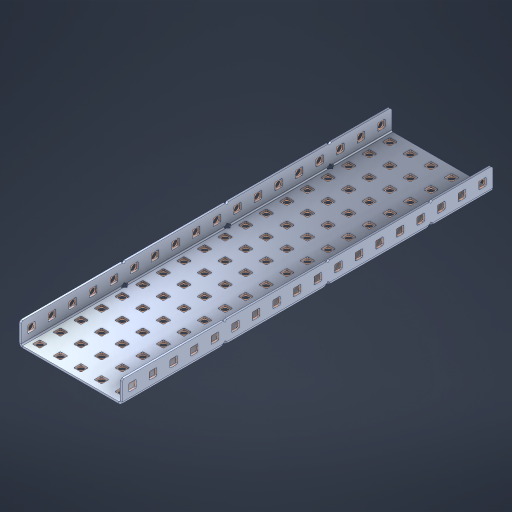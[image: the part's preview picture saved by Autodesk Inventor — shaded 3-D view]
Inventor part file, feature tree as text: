
AUTODESK INVENTOR PART (.ipt)
format: ipt  version: 2023 (Build 270158000, 158)  size: 1,547,264 bytes
history: native  units: in
note: dims shown in document units (in); Inventor stores cm internally (conversion verified against a paired STEP export)
features: other x131, extrude x125, sheet_metal_op x10, sketch x8, mirror x1, pattern_linear x1, chamfer x1
ambient origin geometry x8: Origin, YZ Plane, XZ Plane, XY Plane, X Axis, Y Axis, Z Axis, Center Point
bodies: Solid1 (feature_tree), Body (feature_tree)
feature tree (277):
  other  "Flange Pattern Plane"
  sheet_metal_op  "Flange Pattern"
  sheet_metal_op  "Body Pattern"
  other  "Arc Length"
  mirror  "Notch Mirror"
  pattern_linear  "Notch Pattern"  Spacing1=0.1875in  [1 undecoded]
  chamfer  "End Chamfer"
  extrude  "Half Cut"  Depth=0.0469in
  sketch  "Sketch1"  dims[d0=2.5in]
  other  "Plate1"
  sketch  "Sketch2"  dims[d1=9.0in]
  other  "Plate2"
  sheet_metal_op  "Bend1"
  sheet_metal_op  "Corner1"
  sketch  "Sketch3"  dims[d2=0.0469in]
  other  "Flange Pattern Sketch"
  sketch  "Sketch7"  dims[d3=0.0469in]
  other  "Srf1"
  other  "Srf2"
  sketch  "Sketch8"  dims[d4=0.0234in]
  sketch  "Sketch9"  dims[d5=0.0938in]
  other  "Srf91"
  sheet_metal_op  "Body Pattern Sketch"
  other  "Srf92"
  sketch  "Sketch13"  dims[d6=0.0469in]
  sketch  "Sketch14"  dims[d7=0.5in d8=90.0deg d9=0.0312in d10=0.1875in d11=0.0469in d12=0.0469in d16=0.182in d17=0.02in d18=0.0469in d19=0.0in d20=0.25in d21=0.25in d46=0.172in d47=1.0in d48=0.0in d49=0.182in d50=0.02in d51=0.25in d52=0.25in d53=0.0469in d54=0.0in d55=0.172in d56=1.0in d57=0.0in d60=7.0866in d62=0.5in d63=1.9685in d65=0.5in d85=0.1227in d86=0.1659in d88=0.04in d89=0.0469in d90=0.0in d91=0.04in d92=0.0491in d95=2.5in d96=0.04in d97=0.25in d98=45.0deg d101=0.0in d102=2.497in d131=2.5in d132=7.0866in d134=0.5in d139=0.5in]
  other  "Srf856"
  other  "Srf1310"
  other  "Srf1311"
  other  "Srf1312"
  other  "Srf1376"
  other  "Srf1377"
  other  "Srf1728"
  other  "Srf1755"
  other  "Srf1878"
  other  "Srf1879"
  other  "Srf1880"
  other  "Srf1881"
  other  "Srf1882"
  other  "Srf1883"
  other  "Srf1884"
  other  "Srf1885"
  other  "Srf1886"
  other  "Srf1887"
  other  "Srf1888"
  other  "Srf1889"
  other  "Srf1890"
  other  "Srf1891"
  other  "Srf1892"
  other  "Srf1893"
  other  "Srf1894"
  other  "Srf1895"
  other  "Srf1896"
  other  "Srf1897"
  other  "Srf1898"
  other  "Srf1899"
  other  "Srf1900"
  other  "Srf1901"
  other  "Srf1902"
  other  "Srf1903"
  other  "Srf1904"
  other  "Srf1905"
  other  "Srf1906"
  other  "Srf1942"
  other  "Srf1943"
  other  "Srf1944"
  other  "Srf1945"
  other  "Srf1946"
  other  "Srf1947"
  other  "Srf1948"
  other  "Srf1949"
  other  "Srf1950"
  other  "Srf1951"
  other  "Srf1952"
  other  "Srf1953"
  other  "Srf1954"
  other  "Srf1955"
  other  "Srf1956"
  other  "Srf1957"
  other  "Srf1958"
  other  "Srf1959"
  other  "Srf1960"
  other  "Srf1961"
  other  "Srf1962"
  other  "Srf1963"
  other  "Srf1964"
  other  "Srf1965"
  other  "Srf1966"
  other  "Srf1967"
  other  "Srf1968"
  other  "Srf1969"
  other  "Srf1970"
  other  "Srf2111"
  other  "Srf2146"
  other  "Srf2147"
  other  "Srf2148"
  other  "Srf2149"
  other  "Srf2150"
  other  "Srf2151"
  other  "Srf2152"
  other  "Srf2153"
  other  "Srf2154"
  other  "Srf2155"
  other  "Srf2156"
  other  "Srf2157"
  other  "Srf2158"
  other  "Srf2159"
  other  "Srf2160"
  other  "Srf2161"
  other  "Srf2162"
  other  "Srf2163"
  other  "Srf2164"
  other  "Srf2165"
  other  "Srf2166"
  other  "Srf2167"
  other  "Srf2168"
  other  "Srf2169"
  other  "Srf2170"
  other  "Srf2171"
  other  "Srf2172"
  other  "Srf2173"
  other  "Srf2174"
  other  "Srf2175"
  other  "Srf2176"
  other  "Srf2177"
  other  "Srf2178"
  other  "Srf2179"
  other  "Srf2180"
  other  "Srf2181"
  other  "Srf2182"
  other  "Srf2183"
  other  "Srf2184"
  other  "Srf2185"
  other  "Srf2186"
  other  "Srf2187"
  other  "Srf2188"
  other  "Srf2189"
  other  "Srf2190"
  other  "Srf2191"
  other  "Srf2192"
  other  "Srf2193"
  other  "Srf2194"
  other  "Srf2195"
  other  "Srf2196"
  other  "Srf2197"
  other  "Srf2198"
  other  "Srf2199"
  other  "Srf2200"
  sheet_metal_op  "Flange Stamp"
  sheet_metal_op  "Flange Circle"
  sheet_metal_op  "Body Stamp"
  sheet_metal_op  "Body Circle"
  sheet_metal_op  "Notch"
  extrude  "ExtrusionSrf2"  Depth=0.0469in
  extrude  "ExtrusionSrf92"  Depth=2.5in
  extrude  "ExtrusionSrf856"  Depth=0.02in
  extrude  "ExtrusionSrf1310"  Depth=0.0469in
  extrude  "ExtrusionSrf1311"  TaperAngle=0.0deg  [1 undecoded]
  extrude  "ExtrusionSrf1312"  Depth=0.25in
  extrude  "ExtrusionSrf1376"  Depth=0.25in
  extrude  "ExtrusionSrf1377"  Depth=2.5in
  extrude  "ExtrusionSrf1728"  Depth=2.5in TaperAngle=0.0deg
  extrude  "ExtrusionSrf1755"  Depth=2.5in
  extrude  "ExtrusionSrf1878"  Depth=0.02in
  extrude  "ExtrusionSrf1879"  Depth=0.25in
  extrude  "ExtrusionSrf1880"  Depth=0.25in
  extrude  "ExtrusionSrf1881"  Depth=0.0469in
  extrude  "ExtrusionSrf1882"  TaperAngle=0.0deg  [1 undecoded]
  extrude  "ExtrusionSrf1883"  Depth=2.5in
  extrude  "ExtrusionSrf1884"  Depth=2.5in TaperAngle=0.0deg
  extrude  "ExtrusionSrf1885"  Depth=2.5in
  extrude  "ExtrusionSrf1886"  Depth=2.5in
  extrude  "ExtrusionSrf1887"  Depth=2.5in
  extrude  "ExtrusionSrf1888"  Depth=2.5in
  extrude  "ExtrusionSrf1889"  Depth=2.5in
  extrude  "ExtrusionSrf1890"  Depth=0.0469in
  extrude  "ExtrusionSrf1891"  TaperAngle=0.0deg  [1 undecoded]
  extrude  "ExtrusionSrf1892"  Depth=2.5in
  extrude  "ExtrusionSrf1893"  Depth=2.5in
  extrude  "ExtrusionSrf1894"  Depth=2.5in
  extrude  "ExtrusionSrf1895"  Depth=0.25in TaperAngle=45.0deg
  extrude  "ExtrusionSrf1896"  TaperAngle=0.0deg  [1 undecoded]
  extrude  "ExtrusionSrf1897"  Depth=2.5in
  extrude  "ExtrusionSrf1898"  Depth=2.5in
  extrude  "ExtrusionSrf1899"  Depth=2.5in
  extrude  "ExtrusionSrf1900"  Depth=2.5in
  extrude  "ExtrusionSrf1901"  Depth=2.5in
  extrude  "ExtrusionSrf1902"  [1 undecoded]
  extrude  "ExtrusionSrf1903"  [1 undecoded]
  extrude  "ExtrusionSrf1904"  [1 undecoded]
  extrude  "ExtrusionSrf1905"  [1 undecoded]
  extrude  "ExtrusionSrf1906"  [1 undecoded]
  extrude  "ExtrusionSrf1942"  [1 undecoded]
  extrude  "ExtrusionSrf1943"  [1 undecoded]
  extrude  "ExtrusionSrf1944"  [1 undecoded]
  extrude  "ExtrusionSrf1945"  [1 undecoded]
  extrude  "ExtrusionSrf1946"  [1 undecoded]
  extrude  "ExtrusionSrf1947"  [1 undecoded]
  extrude  "ExtrusionSrf1948"  [1 undecoded]
  extrude  "ExtrusionSrf1949"  [1 undecoded]
  extrude  "ExtrusionSrf1950"  [1 undecoded]
  extrude  "ExtrusionSrf1951"  [1 undecoded]
  extrude  "ExtrusionSrf1952"  [1 undecoded]
  extrude  "ExtrusionSrf1953"  [1 undecoded]
  extrude  "ExtrusionSrf1954"  [1 undecoded]
  extrude  "ExtrusionSrf1955"  [1 undecoded]
  extrude  "ExtrusionSrf1956"  [1 undecoded]
  extrude  "ExtrusionSrf1957"  [1 undecoded]
  extrude  "ExtrusionSrf1958"  [1 undecoded]
  extrude  "ExtrusionSrf1959"  [1 undecoded]
  extrude  "ExtrusionSrf1960"  [1 undecoded]
  extrude  "ExtrusionSrf1961"  [1 undecoded]
  extrude  "ExtrusionSrf1962"  [1 undecoded]
  extrude  "ExtrusionSrf1963"  [1 undecoded]
  extrude  "ExtrusionSrf1964"  [1 undecoded]
  extrude  "ExtrusionSrf1965"  [1 undecoded]
  extrude  "ExtrusionSrf1966"  [1 undecoded]
  extrude  "ExtrusionSrf1967"  [1 undecoded]
  extrude  "ExtrusionSrf1968"  [1 undecoded]
  extrude  "ExtrusionSrf1969"  [1 undecoded]
  extrude  "ExtrusionSrf1970"  [1 undecoded]
  extrude  "ExtrusionSrf2111"  [1 undecoded]
  extrude  "ExtrusionSrf2146"  [1 undecoded]
  extrude  "ExtrusionSrf2147"  [1 undecoded]
  extrude  "ExtrusionSrf2148"  [1 undecoded]
  extrude  "ExtrusionSrf2149"  [1 undecoded]
  extrude  "ExtrusionSrf2150"  [1 undecoded]
  extrude  "ExtrusionSrf2151"  [1 undecoded]
  extrude  "ExtrusionSrf2152"  [1 undecoded]
  extrude  "ExtrusionSrf2153"  [1 undecoded]
  extrude  "ExtrusionSrf2154"  [1 undecoded]
  extrude  "ExtrusionSrf2155"  [1 undecoded]
  extrude  "ExtrusionSrf2156"  [1 undecoded]
  extrude  "ExtrusionSrf2157"  [1 undecoded]
  extrude  "ExtrusionSrf2158"  [1 undecoded]
  extrude  "ExtrusionSrf2159"  [1 undecoded]
  extrude  "ExtrusionSrf2160"  [1 undecoded]
  extrude  "ExtrusionSrf2161"  [1 undecoded]
  extrude  "ExtrusionSrf2162"  [1 undecoded]
  extrude  "ExtrusionSrf2163"  [1 undecoded]
  extrude  "ExtrusionSrf2164"  [1 undecoded]
  extrude  "ExtrusionSrf2165"  [1 undecoded]
  extrude  "ExtrusionSrf2166"  [1 undecoded]
  extrude  "ExtrusionSrf2167"  [1 undecoded]
  extrude  "ExtrusionSrf2168"  [1 undecoded]
  extrude  "ExtrusionSrf2169"  [1 undecoded]
  extrude  "ExtrusionSrf2170"  [1 undecoded]
  extrude  "ExtrusionSrf2171"  [1 undecoded]
  extrude  "ExtrusionSrf2172"  [1 undecoded]
  extrude  "ExtrusionSrf2173"  [1 undecoded]
  extrude  "ExtrusionSrf2174"  [1 undecoded]
  extrude  "ExtrusionSrf2175"  [1 undecoded]
  extrude  "ExtrusionSrf2176"  [1 undecoded]
  extrude  "ExtrusionSrf2177"  [1 undecoded]
  extrude  "ExtrusionSrf2178"  [1 undecoded]
  extrude  "ExtrusionSrf2179"  [1 undecoded]
  extrude  "ExtrusionSrf2180"  [1 undecoded]
  extrude  "ExtrusionSrf2181"  [1 undecoded]
  extrude  "ExtrusionSrf2182"  [1 undecoded]
  extrude  "ExtrusionSrf2183"  [1 undecoded]
  extrude  "ExtrusionSrf2184"  [1 undecoded]
  extrude  "ExtrusionSrf2185"  [1 undecoded]
  extrude  "ExtrusionSrf2186"  [1 undecoded]
  extrude  "ExtrusionSrf2187"  [1 undecoded]
  extrude  "ExtrusionSrf2188"  [1 undecoded]
  extrude  "ExtrusionSrf2189"  [1 undecoded]
  extrude  "ExtrusionSrf2190"  [1 undecoded]
  extrude  "ExtrusionSrf2191"  [1 undecoded]
  extrude  "ExtrusionSrf2192"  [1 undecoded]
  extrude  "ExtrusionSrf2193"  [1 undecoded]
  extrude  "ExtrusionSrf2194"  [1 undecoded]
  extrude  "ExtrusionSrf2195"  [1 undecoded]
  extrude  "ExtrusionSrf2196"  [1 undecoded]
  extrude  "ExtrusionSrf2197"  [1 undecoded]
  extrude  "ExtrusionSrf2198"  [1 undecoded]
  extrude  "ExtrusionSrf2199"  [1 undecoded]
  extrude  "ExtrusionSrf2200"  [1 undecoded]
note: 95 required parameter values undecoded (feature->parameter linkage not recoverable at this tier; creation-order binding heuristic only, values carry confidence <= 0.55)
